# Revit family: ADB Fourneaux Electrique L700
name_source: partatom
category: Equipement spécialisé
units: mm (PartAtom-declared; Revit-internal decimal feet)

## family parameters
Basée sur le plan de construction = Non
Conserver l'orientation des annotations = Non
Cote de connecteur circulaire = Utiliser le diamètre
Couper avec des vides une fois chargée = Non
Numéro OmniClass = 23.40.40.14.17.11
Partagée = Non
Repère de localisation dans la pièce = Non
Titre OmniClass = Cookers, Ovens, Stoves
Toujours verticalement = Oui
Type d'élément = Normal

## types (2) — shared parameters
B = 180 mm  [stored 0.590551 ft]
C = 390 mm  [stored 1.27953 ft]
Commentaires du type = Gamme Ambassade - Fourneaux électriques
Fabricant = Société Industrielle de Lacanche
URL = https://www.ambassade-de-bourgogne.com
zero-valued in all types: Elévation par défaut

## per-type parameters (varying)
| type | CE 741 E | CE 741 VTR | Description | Modèle | Pbase | Poids net à vide | Table |
| 4 foyers radiants 1 four Gastronorme - CE 741 VTR | Non | Oui | Fourneau électrique - 4 foyers radiants 1 four électrique Gastronorme | CE 741 VTR | 11500 W | 86.00 kg | CE741 VTR_4 foyers radiants |
| 4 plaques électriques 1 four Gastronorme - CE 741 E | Oui | Non | Fourneau électrique - 4 plaques électriques 1 four électrique Gastronorme | CE 741 E | 10100 W | 93.00 kg | CE741E _4 plaques électriques |

note: [stored X ft] marks values corroborated as IEEE doubles in the binary element streams (Revit-internal decimal feet)
